# Revit family: F1120-C-T
name_source: partatom
category: Plumbing Fixtures
units: mm (PartAtom-declared; Revit-internal decimal feet)

## family parameters
Classification Number = 23.45.55.21
Cut with Voids When Loaded = No
Enable Cutting in Views = No
Host = Face
Maintain Annotation Orientation = No
Part Type = Normal
Room Calculation Point = No
Round Connector Dimension = Use Radius
Shared = No

## types (15) — shared parameters
Description = TERRACE DRAIN WITH INTEGRAL DEEP SEAL TRAP
Floor Drain Material = Paint - Sherwin Williams Paint - #952C2A - Bellwood Red
Manufacturer = MIFAB
Model = F1120-C
Top Assembly Diameter = 8 "
URL = WWW.MIFAB.COM
zero-valued in all types: Default Elevation, WFU

## per-type parameters (varying)
| type | Pipe Diameter | Pipe Radius | Strainer Diameter |
| 5" Strainer - 4" Drain | 4 " | 2 " | 5 " |
| 10" Strainer - 2" Drain | 2 " | 1 " | 10 " |
| 5" Strainer - 2" Drain | 2 " | 1 " | 5 " |
| 6" Strainer - 2" Drain | 2 " | 1 " | 6 " |
| 7" Strainer - 2" Drain | 2 " | 1 " | 7 " |
| 8" Strainer - 2" Drain | 2 " | 1 " | 8 " |
| 5" Strainer - 3" Drain | 3 " | 1.5 " | 5 " |
| 6" Strainer - 3" Drain | 3 " | 1.5 " | 6 " |
| 7" Strainer - 3" Drain | 3 " | 1.5 " | 7 " |
| 8" Strainer - 3" Drain | 3 " | 1.5 " | 8 " |
| 10" Strainer - 3" Drain | 3 " | 1.5 " | 10 " |
| 6" Strainer - 4" Drain | 4 " | 2 " | 6 " |
| 7" Strainer - 4" Drain | 4 " | 2 " | 7 " |
| 8" Strainer - 4" Drain | 4 " | 2 " | 8 " |
| 10" Strainer - 4" Drain | 4 " | 2 " | 10 " |

## geometry (parser evidence)
native form markers: Blend x5, Sweep x2
no freeform markers — native parametric forms only
